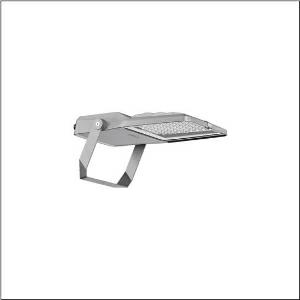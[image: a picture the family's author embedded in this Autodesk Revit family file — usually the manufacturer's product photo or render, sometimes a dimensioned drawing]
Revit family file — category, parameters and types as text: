
# Revit family: floodlight_fl_21_iq_mini___pl64_5xa7772d5e1a_506a
name_source: partatom
category: Lighting Fixtures
units: mm (PartAtom-declared; Revit-internal decimal feet)

## family parameters
Cut with Voids When Loaded = No
Host = Face
Light Source = No
Part Type = Normal
Room Calculation Point = No
Round Connector Dimension = Use Diameter
Shared = No

## types (1)
- --- (1 x LED, 16070 lm, 143 W, 4000K)
    Apparent Load = 143 VA
    CIE Flux Codes = 28 80 98 100 100
    Color Rendering = 80
    Color Temperature = 4000K
    Default Elevation = 1800 mm
    Description = Floodlight FL 21 iQ mini, floodlight, primary light control with lens, of PMMA, primary optical cover: protective disc, of toughened safety glass, transparent, light distribution: PL64, light emission: direct distribution, installation type: surface-mounted, lamps: LED, High Power LED, rated values: 16.070lm | 143W | 112,4lm/W (begin service life); end service life: 16.070lm | 151,6W; at 50% lumin. flux: 8.035lm | 60,6W | 132,6lm/W, colour temperature: 4000K, colour rendering: CRI > 80, light colour: 840, light setting 1 begin service life: 100% | 16.070lm | 143W | 112,4lm/W | 4.000K, light setting 1 end service life: 151,6W, further light settings possible, control: Street-Remote, Auto-Match, Temp-Guard, Night-Set, Smart-Wire, Desk-Remote (wireless, voltage-free reading and setting of iQ features in the workshop via application-optimized NFC function/RFID function), optimised constant luminous flux control (CLO 2.0), pre-setting: linear dimming characteristic, with terminal, 6-pole, mains connection: 220..240V, AC, 50/60Hz, luminaire housing, of diecast aluminium, powder-coated, SITECO metallic grey (DB 702S), corrosivity category C5 mid according to DIN EN ISO 12944suitable for swimming poolschlorine-resistant, sealing non-destructively replaceable, mounting bracket, of steel, galvanised, powder-coated, SITECO metallic grey (DB 702S), protection rating (complete): IP66, insulation class (complete): insulation class II (safety insulation), certification: CE, ENEC, VDE, protection symbol: D, impact resistance: IK08, permissible operating ambient temperature: -40..+40°C, permissible operating ambient temperature for outdoor applications: -40..+50°C, standard: DIN EN 12944, LABS conformity tested according to VDMA 24364:2018-05, packaging unit: 1 piece

Light Distribution: PL64
    Height = 70 mm
    Lamp = 1 x LED
    Lamp Light Flux = 16070 lm
    Lamp Power = 143 W
    Lamp count = 1
    Length = 485 mm
    Luminous efficacy = 112 lm/W
    Manufacturer = Siteco
    ModVariant = No
    Model = 5XA7772D5E1A
    Number of Poles = 1
    OnlyDefault = Yes
    Power Factor = 1
    Product Name = Floodlight FL 21 iQ mini | PL64
    Product group = floodlight | pylon annexe
    ProductGroupID = 6201
    Protection Class = Protection class II
    Protection Degree = IP 66
    RLX_Detail_Level = 1
    RLX_Emergency_Light_Flux = 0 lm
    RLX_Emergency_Type = 0
    RLX_Emergency_Type_DB = No
    RlxData = <blob elided: 96909 chars, md5=cb345416>
    Socket = socket
    Standby Power = 0 W
    System Light Flux = 16070 lm
    System Power = 143 W
    Type Comments = factory setting: luminous flux: 100 % | dim-lin: 254 | 730 mA
    Type Image = l_1006845.jpg
    URL = http://relux.com
    VarID = @adj_165089
    Voltage = 0 V
    Weight = 0.00 kg
    Width = 337 mm

## geometry (parser evidence)
native form markers: Blend x4, Sweep x13
no freeform markers — native parametric forms only
